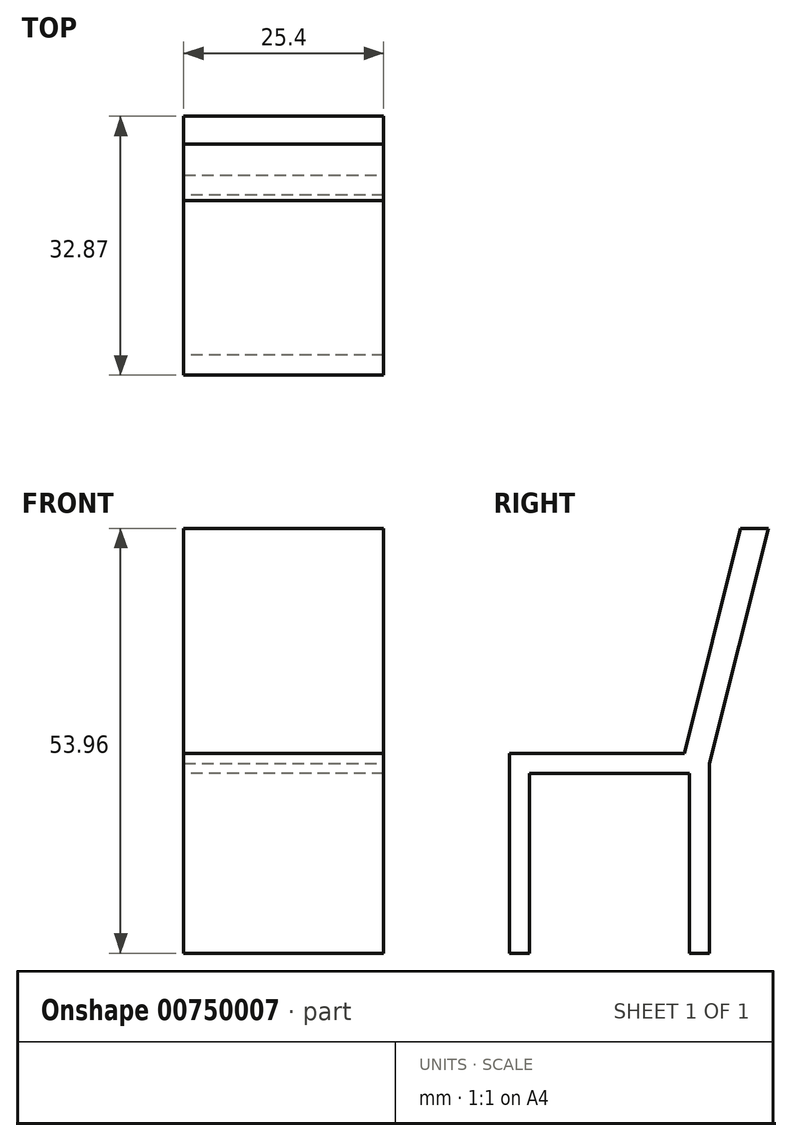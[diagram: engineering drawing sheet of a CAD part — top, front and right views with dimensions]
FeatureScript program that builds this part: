
annotation { "Feature Type Name" : "Feature", "Feature Type Description" : "" }
export const myFeature = defineFeature(function(context is Context, id is Id, definition is map)
    precondition{}
    {
        {
            var Q0;
            Q0=qCreatedBy(makeId("Top.planeOp"),FACE);
            var sketch = newSketch(context, id + "F0", { "sketchPlane" : qUnion([Q0])});
            skLineSegment(sketch, "E0.bottom", {"start": v(0, 0) * mm, "end": v(-25.4, 0) * mm});
            skLineSegment(sketch, "E0.top", {"start": v(0, -25.4) * mm, "end": v(-25.4, -25.4) * mm});
            skLineSegment(sketch, "E0.left", {"start": v(0, 0) * mm, "end": v(0, -25.4) * mm});
            skLineSegment(sketch, "E0.right", {"start": v(-25.4, 0) * mm, "end": v(-25.4, -25.4) * mm});
            skSolve(sketch);
        }
        {
            var Q0;
            Q0 = qSketchRegion(id + "F0", true);
            extrude(context, id + "F1", {"entities" : qUnion([Q0]), "depth" : 25.4 * mm, "offsetDistance" : 25.4 * mm});
        }
        {
            var Q0;
            Q0=makeQuery(id+"F1.opExtrude","SWEPT_FACE",FACE,{"disambiguationData":[OSD([sQuery(id+"F0.wireOp",EDGE,"E0.left")])]});
            var Q1;
            Q1=makeQuery(id+"F1.opExtrude","SWEPT_FACE",FACE,{"disambiguationData":[OSD([sQuery(id+"F0.wireOp",EDGE,"E0.right")])]});
            var Q2;
            Q2=makeQuery(id+"F1.opExtrude","CAP_FACE",FACE,{"disambiguationData":[OSD([sQuery(id+"F0.wireOp",EDGE,"E0.bottom"),sQuery(id+"F0.wireOp",EDGE,"E0.top"),sQuery(id+"F0.wireOp",EDGE,"E0.left"),sQuery(id+"F0.wireOp",EDGE,"E0.right")])],"isStart":true});
            shell(context, id + "F2", {"entities" : qUnion([Q0, Q1, Q2]), "thickness" : 2.54 * mm});
        }
        {
            var Q0;
            Q0=qCreatedBy(makeId("Right.planeOp"),FACE);
            var sketch = newSketch(context, id + "F3", { "sketchPlane" : qUnion([Q0])});
            skLineSegment(sketch, "E1", {"start": v(0, 24.09) * mm, "end": v(7.47, 53.96) * mm});
            skLineSegment(sketch, "E2", {"start": v(7.47, 53.96) * mm, "end": v(3.92, 53.96) * mm});
            skLineSegment(sketch, "E3", {"start": v(3.92, 53.96) * mm, "end": v(-3.53, 24.17) * mm});
            skLineSegment(sketch, "E4", {"start": v(-3.53, 24.17) * mm, "end": v(0, 24.09) * mm});
            skSolve(sketch);
        }
        {
            var Q0;
            Q0=makeQuery(id+"F3.imprint","IMPRINT",FACE,{"disambiguationData":[TD([[makeQuery(id+"F3.imprint","IMPRINT",EDGE,{"derivedFrom":sQuery(id+"F3.wireOp",EDGE,"E1")}),1.0]])]});
            extrude(context, id + "F4", {"entities" : qUnion([Q0]), "operationType" : NewBodyOperationType.ADD, "oppositeDirection" : true, "depth" : 25.4 * mm, "offsetDistance" : 25.4 * mm});
        }
    });
